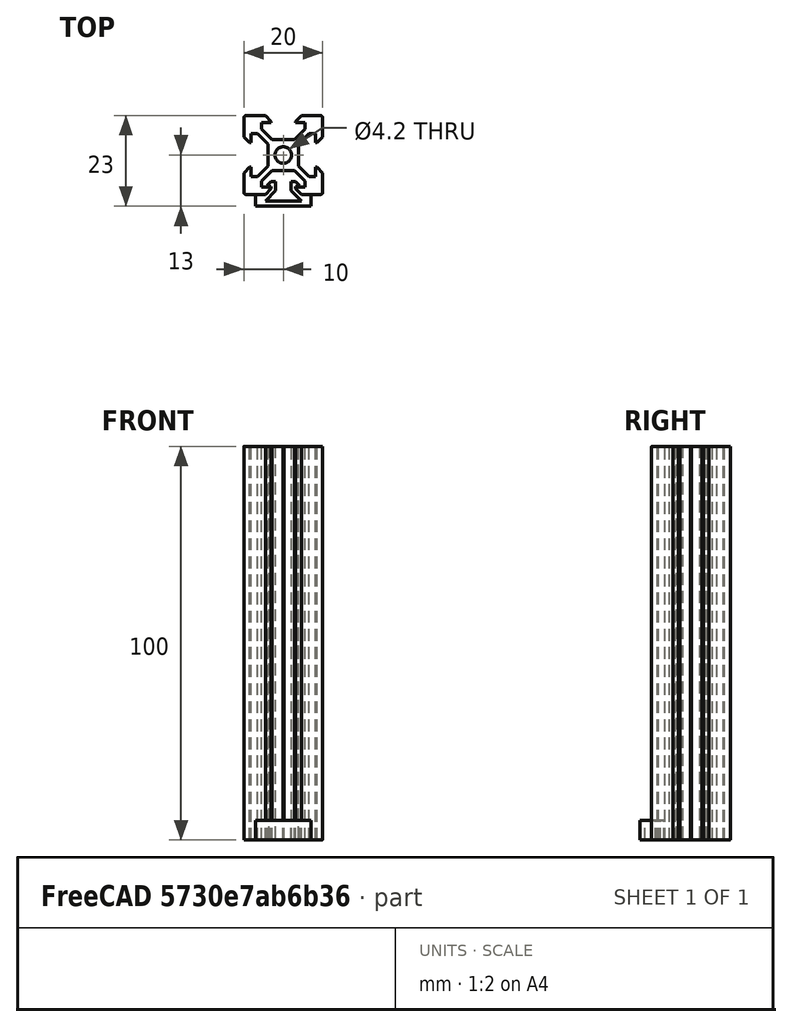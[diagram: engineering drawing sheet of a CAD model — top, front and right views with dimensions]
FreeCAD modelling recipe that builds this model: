
FCSTD DOCUMENT  (FreeCAD 0.20R27861 (Git))
Label: 2020 cable clamp
License: All rights reserved
LicenseURL: http://en.wikipedia.org/wiki/All_rights_reserved
objects: Part::Feature×1, PartDesign::SubShapeBinder×1, Sketcher::SketchObject×1, PartDesign::Pad×1, PartDesign::Body×1
note: 6 computed .brp shape members not serialized (recipe doc carries the construction recipe); baked Part::Feature solids carry a one-line shape summary decoded from their .brp

FEATURE [Part::Feature] Part__Feature  label="2020-100"
  shape: bbox 20 x 20 x 100 mm, 67 faces (baked)
FEATURE [PartDesign::SubShapeBinder] Binder
  BindCopyOnChange = 0
  BindMode = 0
  ClaimChildren = false
  Context = -> Body [Binder.]
  Fuse = false
  MakeFace = true
  PartialLoad = false
  Relative = true
  Support = -> [Part__Feature]
  _Version = 2
FEATURE [Sketcher::SketchObject] Sketch
  ExternalGeometry = -> [Binder]
  FullyConstrained = true
  MapMode = 5
  Support = -> [XY_Plane]
  sketch-geometry (27):
    g0: LineSegment StartX=-4.58 StartY=-10 StartZ=0 EndX=-3.125 EndY=-8.545 EndZ=0
    g1: LineSegment StartX=-3.125 StartY=-8.545 StartZ=0 EndX=-3.125 EndY=-8 EndZ=0
    g2: LineSegment StartX=-3.125 StartY=-8 StartZ=0 EndX=-4.125 EndY=-8 EndZ=0
    g3: LineSegment StartX=4.58 StartY=-10 StartZ=0 EndX=3.125 EndY=-8.545 EndZ=0
    g4: LineSegment StartX=3.125 StartY=-8 StartZ=0 EndX=4.125 EndY=-8 EndZ=0
    g5: LineSegment StartX=4.58 StartY=-11.6971 StartZ=0 EndX=-4.58 EndY=-11.6971 EndZ=0
    g6: LineSegment StartX=-4.58 StartY=-10 StartZ=0 EndX=-7 EndY=-10 EndZ=0
    g7: LineSegment StartX=-7 StartY=-10 StartZ=0 EndX=-7 EndY=-13 EndZ=0
    g8: LineSegment StartX=-7 StartY=-13 StartZ=0 EndX=7 EndY=-13 EndZ=0
    g9: LineSegment StartX=7 StartY=-13 StartZ=0 EndX=7 EndY=-10 EndZ=0
    g10: LineSegment StartX=7 StartY=-10 StartZ=0 EndX=4.58 EndY=-10 EndZ=0
    g11: LineSegment StartX=3.125 StartY=-8.545 StartZ=0 EndX=3.125 EndY=-8 EndZ=0
    g12: LineSegment StartX=-1.925 StartY=-6.8 StartZ=0 EndX=-1.925 EndY=-9.04206 EndZ=0
    g13: LineSegment StartX=-1.925 StartY=-9.04206 StartZ=0 EndX=-4.58 EndY=-11.6971 EndZ=0
    g14: LineSegment StartX=1.925 StartY=-6.8 StartZ=0 EndX=1.925 EndY=-9.04206 EndZ=0
    g15: LineSegment StartX=1.925 StartY=-9.04206 StartZ=0 EndX=4.58 EndY=-11.6971 EndZ=0
    g16: LineSegment StartX=-4.125 StartY=-8 StartZ=0 EndX=-4.125 EndY=-8.2 EndZ=0
    g17: LineSegment StartX=4.125 StartY=-8 StartZ=0 EndX=4.125 EndY=-8.2 EndZ=0
    g18: LineSegment StartX=-4.125 StartY=-8 StartZ=0 EndX=-4.125 EndY=-7.8 EndZ=0
    g19: LineSegment StartX=-4.125 StartY=-7.8 StartZ=0 EndX=-3.125 EndY=-6.8 EndZ=0
    g20: LineSegment StartX=-3.125 StartY=-6.8 StartZ=0 EndX=-1.925 EndY=-6.8 EndZ=0
    g21: LineSegment StartX=1.925 StartY=-6.8 StartZ=0 EndX=3.125 EndY=-6.8 EndZ=0
    g22: LineSegment StartX=3.125 StartY=-6.8 StartZ=0 EndX=4.125 EndY=-7.8 EndZ=0
    g23: LineSegment StartX=4.125 StartY=-7.8 StartZ=0 EndX=4.125 EndY=-8 EndZ=0
    g24: LineSegment StartX=-3.125 StartY=-8.545 StartZ=0 EndX=-2.27647 EndY=-9.39353 EndZ=0
    g25: LineSegment StartX=-3.125 StartY=-8 StartZ=0 EndX=-1.925 EndY=-8 EndZ=0
    g26: LineSegment StartX=-3.125 StartY=-8 StartZ=0 EndX=-3.125 EndY=-6.8 EndZ=0
  constraints (78):
    c: Coincident(g1,g0)
    c: Vertical(g1)
    c: Coincident(g2,g1)
    c: Horizontal(g2)
    c: Horizontal(g4)
    c: Horizontal(g5)
    c: Coincident(g6,g0)
    c: Horizontal(g6)
    c: Coincident(g7,g6)
    c: Vertical(g7)
    c: Coincident(g8,g7)
    c: Horizontal(g8)
    c: Coincident(g9,g8)
    c: Vertical(g9)
    c: Coincident(g10,g9)
    c: Coincident(g10,g3)
    c: Horizontal(g10)
    c: Coincident(g11,g3)
    c: Coincident(g11,g4)
    c: Vertical(g11)
    c: Parallel(g0,g-3)
    c: Parallel(g3,g-4)
    c: Horizontal(g-3,g0)
    c: Horizontal(g-4,g3)
    c: DistanceX(g8,g8) = 14
    c: DistanceY(g9,g9) = 3
    c: Vertical(g12)
    c: Coincident(g13,g12)
    c: Vertical(g14)
    c: Coincident(g15,g14)
    c: Coincident(g5,g13)
    c: Coincident(g5,g15)
    c: Equal(g6,g10)
    c: Vertical(g5,g3)
    c: Parallel(g13,g0)
    c: Parallel(g15,g3)
    c: Equal(g11,g1)
    c: DistanceX(g2,g-3) = 1
    c: Coincident(g16,g2)
    c: PointOnObject(g16,g-5)
    c: Vertical(g16)
    c: Coincident(g17,g4)
    c: PointOnObject(g17,g-6)
    c: Vertical(g17)
    c: Equal(g4,g2)
    c: Equal(g12,g14)
    c: Coincident(g18,g2)
    c: Coincident(g19,g18)
    c: Coincident(g20,g19)
    c: Horizontal(g20)
    c: Coincident(g21,g14)
    c: Horizontal(g21)
    c: Coincident(g22,g21)
    c: Coincident(g23,g22)
    c: Vertical(g23)
    c: Coincident(g4,g23)
    c: Equal(g18,g23)
    c: Parallel(g0,g19)
    c: Parallel(g22,g3)
    c: Vertical(g18)
    c: Coincident(g20,g12)
    c: Coincident(g24,g0)
    c: PointOnObject(g24,g13)
    c: Perpendicular(g13,g24)
    c: Coincident(g25,g1)
    c: PointOnObject(g25,g12)
    c: Horizontal(g25)
    c: Equal(g24,g25)
    c: Coincident(g26,g1)
    c: Vertical(g26)
    c: Equal(g26,g25)
    c: Equal(g13,g15)
    c: DistanceY(g26,g26) = 1.2
    c: Equal(g20,g21)
    c: DistanceY(g16,g16) = 0.2
    c: Coincident(g0,g-3)
    c: Coincident(g3,g-4)
    c: Coincident(g26,g19)
FEATURE [PartDesign::Pad] Pad
  Direction = (0,0,1)
  Length = 5
  Length2 = 10
  Profile = -> Sketch
  ReferenceAxis = -> Sketch [N_Axis]
  Refine = true
  Type = 0
FEATURE [PartDesign::Body] Body
  Group = -> [Binder,Sketch,Pad]
  Origin = -> Origin
  Tip = -> Pad
